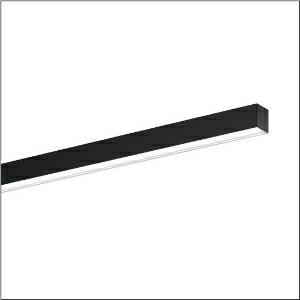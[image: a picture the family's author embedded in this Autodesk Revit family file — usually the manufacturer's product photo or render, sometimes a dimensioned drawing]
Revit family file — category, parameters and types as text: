
# Revit family: silica_r__21_51mx20da32bb_5abe
name_source: partatom
category: Lighting Fixtures
units: mm (PartAtom-declared; Revit-internal decimal feet)

## family parameters
Cut with Voids When Loaded = No
Host = Face
Light Source = No
Part Type = Normal
Room Calculation Point = No
Round Connector Dimension = Use Diameter
Shared = No

## types (1)
- --- (1 x LED, 2400 lm, 16.1 W, 3000K)
    Apparent Load = 16 VA
    CIE Flux Codes = 48 79 96 100 100
    Color Rendering = 80
    Color Temperature = 3000K
    Default Elevation = 1800 mm
    Description = Silica® 21, office luminaire, primary optical cover: cover, of PMMA, opal, light emission: direct distribution, primary light characteristic: symmetric, installation type: surface-mounted, LED, rated luminous flux: 2.400lm, luminous efficacy: 149lm/W, light colour: 830, colour temperature: 3000K, control gear: DALI 2, with terminal, 3+2-pole, max. 2.5mm², mains connection: 220..240V, AC, 50/60Hz, rated input power: 16.1W, luminaire housing, of aluminium, matt jet black (RAL 9005), length: 1.204mm, width: 53mm, height: 53mm, protection rating (complete): IP20, insulation class (complete): insulation class I (protective earthing), certification: CE, permissible operating ambient temperature: 0..+35°C, standard: EN 50419, packaging unit: 1 piece
    Height = 53 mm
    Lamp = 1 x LED
    Lamp Light Flux = 2400 lm
    Lamp Power = 16.1 W
    Lamp count = 1
    Length = 1204 mm
    Luminous efficacy = 149 lm/W
    Manufacturer = Siteco
    ModVariant = No
    Model = 51MX20DA32BB
    Mounting Place = Ceiling
    Mounting Type = Surface mounted
    Number of Poles = 1
    OnlyDefault = Yes
    Power Factor = 1
    Product Name = Silica® 21
    Product group = office luminaire | ceiling mounted
    ProductGroupID = 302
    Protection Class = Protection class I
    Protection Degree = IP 20
    RLX_Detail_Level = 1
    RLX_Emergency_Light_Flux = 0 lm
    RLX_Emergency_Type = 0
    RLX_Emergency_Type_DB = No
    RlxData = <blob elided: 28829 chars, md5=7a7e3f9b>
    Socket = socket
    Standby Power = 0 W
    System Light Flux = 2400 lm
    System Power = 16 W
    Type Comments = factory setting: luminous flux: 100 % | dim-lin: 254 | 233 mA
    Type Image = l_1335925.jpg
    URL = http://relux.com
    VarID = @adj_007583
    Voltage = 0 V
    Weight = 0.00 kg
    Width = 53 mm

## geometry (parser evidence)
native form markers: Blend x4, Sweep x11
no freeform markers — native parametric forms only
